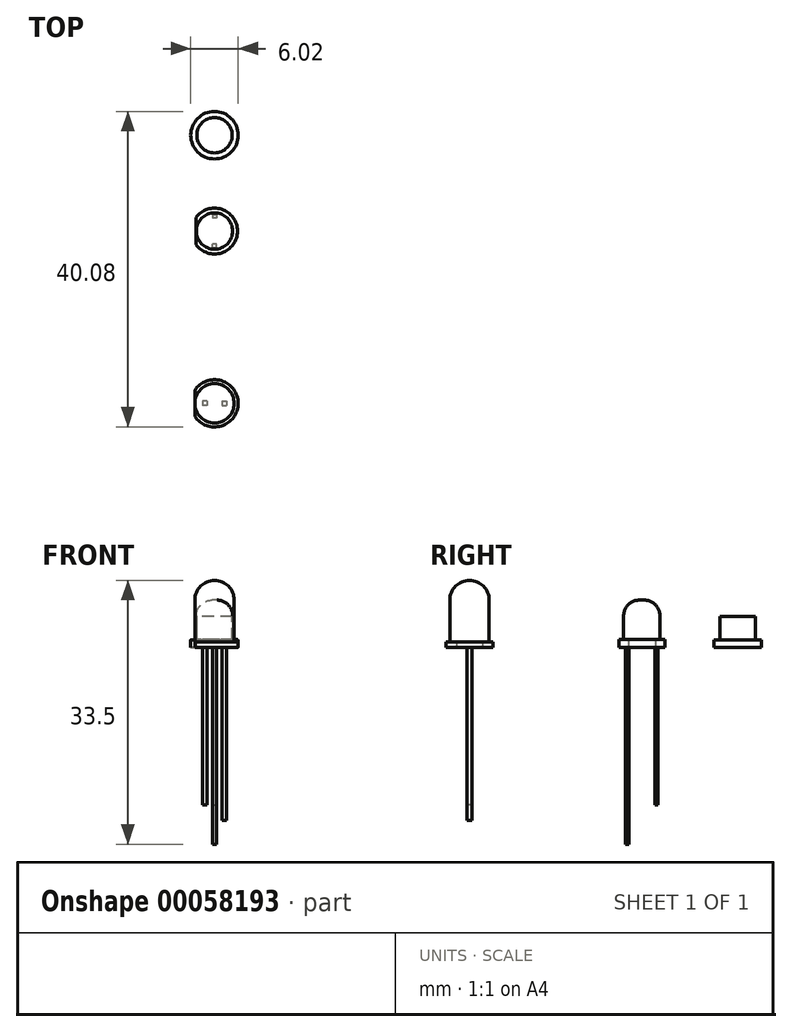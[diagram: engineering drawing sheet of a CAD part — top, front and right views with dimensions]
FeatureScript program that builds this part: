
annotation { "Feature Type Name" : "Feature", "Feature Type Description" : "" }
export const myFeature = defineFeature(function(context is Context, id is Id, definition is map)
    precondition{}
    {
        {
            var Q0;
            Q0=qCreatedBy(makeId("Top.planeOp"),FACE);
            var sketch = newSketch(context, id + "F0", { "sketchPlane" : qUnion([Q0])});
            skCircle(sketch, "E0", {"center": v(0, 0) * mm, "radius": 2.5 * mm});
            skSolve(sketch);
        }
        {
            var Q0;
            Q0=qSketchRegion(id+"F0",true);
            extrude(context, id + "F1", {"entities" : qUnion([Q0]), "depth" : 6 * mm});
        }
        {
            var Q0;
            Q0=makeQuery(id+"F1.opExtrude","CAP_FACE",FACE,{"disambiguationData":[OSD([sQuery(id+"F0.wireOp",EDGE,"E0")])],"isStart":false});
            var sketch = newSketch(context, id + "F2", { "sketchPlane" : qUnion([Q0])});
            skLineSegment(sketch, "E1", {"start": v(0, -2.5) * mm, "end": v(0, 2.5) * mm});
            skArc(sketch, "E2", {"start": v(0, 2.5) * mm, "mid": v(-2.5, 0) * mm, "end": v(0, -2.5) * mm});
            skSolve(sketch);
        }
        {
            var Q0;
            Q0=qSketchRegion(id+"F2",true);
            var Q1;
            Q1=sQuery(id+"F2.wireOp",EDGE,"E1");
            revolve(context, id + "F3", {"operationType" : NewBodyOperationType.ADD, "entities" : qUnion([Q0]), "axis" : qUnion([Q1]), "revolveType" : RevolveType.FULL});
        }
        {
            var Q0;
            Q0=makeQuery(id+"F1.opExtrude","CAP_FACE",FACE,{"disambiguationData":[OSD([sQuery(id+"F0.wireOp",EDGE,"E0")])],"isStart":true});
            var sketch = newSketch(context, id + "F4", { "sketchPlane" : qUnion([Q0])});
            skArc(sketch, "E3.0", {"start": v(-2.5, -1.66) * mm, "mid": v(3, 0) * mm, "end": v(-2.5, 1.66) * mm});
            skLineSegment(sketch, "E4", {"start": v(-2.5, -1.66) * mm, "end": v(-2.5, 1.66) * mm});
            skSolve(sketch);
        }
        {
            var Q0;
            Q0=qSketchRegion(id+"F4",true);
            extrude(context, id + "F5", {"entities" : qUnion([Q0]), "operationType" : NewBodyOperationType.ADD, "oppositeDirection" : true, "depth" : .7 * mm});
        }
        {
            var Q0;
            Q0=makeQuery(id+"F5.boolean.opBoolean","MERGE",FACE,{"derivedFrom":[makeQuery(id+"F1.opExtrude","CAP_FACE",FACE,{"disambiguationData":[OSD([sQuery(id+"F0.wireOp",EDGE,"E0")])],"isStart":true}),makeQuery(id+"F5.opExtrude","CAP_FACE",FACE,{"disambiguationData":[OSD([sQuery(id+"F4.wireOp",EDGE,"E3.0"),sQuery(id+"F4.wireOp",EDGE,"E4")])],"isStart":true})]});
            var sketch = newSketch(context, id + "F6", { "sketchPlane" : qUnion([Q0])});
            skLineSegment(sketch, "E5.rect.bottom", {"start": v(0.95, -0.3) * mm, "end": v(1.55, -0.3) * mm});
            skLineSegment(sketch, "E5.rect.top", {"start": v(0.95, 0.3) * mm, "end": v(1.55, 0.3) * mm});
            skLineSegment(sketch, "E5.rect.left", {"start": v(0.95, -0.3) * mm, "end": v(0.95, 0.3) * mm});
            skLineSegment(sketch, "E5.rect.right", {"start": v(1.55, -0.3) * mm, "end": v(1.55, 0.3) * mm});
            skPoint(sketch, "E5.rect.middle", {"position": v(1.25, 0) * mm});
            skLineSegment(sketch, "E6.rect.bottom", {"start": v(-0.95, -0.3) * mm, "end": v(-1.55, -0.3) * mm});
            skLineSegment(sketch, "E6.rect.top", {"start": v(-0.95, 0.3) * mm, "end": v(-1.55, 0.3) * mm});
            skLineSegment(sketch, "E6.rect.left", {"start": v(-0.95, -0.3) * mm, "end": v(-0.95, 0.3) * mm});
            skLineSegment(sketch, "E6.rect.right", {"start": v(-1.55, -0.3) * mm, "end": v(-1.55, 0.3) * mm});
            skPoint(sketch, "E6.rect.middle", {"position": v(-1.25, 0) * mm});
            skLineSegment(sketch, "E7", {"start": v(1.55, -0.3) * mm, "end": v(0.95, 0.3) * mm, "construction": true});
            skLineSegment(sketch, "E8", {"start": v(1.55, 0.3) * mm, "end": v(0.95, -0.3) * mm, "construction": true});
            skLineSegment(sketch, "E9", {"start": v(-0.95, -0.3) * mm, "end": v(-1.55, 0.3) * mm, "construction": true});
            skLineSegment(sketch, "E10", {"start": v(-0.95, 0.3) * mm, "end": v(-1.55, -0.3) * mm, "construction": true});
            skLineSegment(sketch, "E11", {"start": v(1.25, 0) * mm, "end": v(-1.25, 0) * mm, "construction": true});
            skSolve(sketch);
        }
        {
            var Q0;
            Q0=qSketchRegion(id+"F6",true);
            extrude(context, id + "F7", {"entities" : qUnion([Q0]), "operationType" : NewBodyOperationType.ADD, "depth" : 20 * mm});
        }
        {
            var Q0;
            Q0=makeQuery(id+"F7.opExtrude","CAP_FACE",FACE,{"disambiguationData":[OSD([sQuery(id+"F6.wireOp",EDGE,"E5.rect.bottom"),sQuery(id+"F6.wireOp",EDGE,"E5.rect.top"),sQuery(id+"F6.wireOp",EDGE,"E5.rect.left"),sQuery(id+"F6.wireOp",EDGE,"E5.rect.right")])],"isStart":false});
            extrude(context, id + "F8", {"entities" : qUnion([Q0]), "operationType" : NewBodyOperationType.ADD, "depth" : 2 * mm});
        }
        {
            var Q0;
            Q0=qCreatedBy(makeId("Top.planeOp"),FACE);
            var sketch = newSketch(context, id + "F9", { "sketchPlane" : qUnion([Q0])});
            skCircle(sketch, "E12", {"center": v(7.44, 15.47) * mm, "radius": 4.08 * mm});
            skSolve(sketch);
        }
        {
            var Q0;
            Q0=makeQuery(id+"F9.imprint","IMPRINT",FACE,{"disambiguationData":[TD([[makeQuery(id+"F9.imprint","IMPRINT",EDGE,{"derivedFrom":sQuery(id+"F9.wireOp",EDGE,"E12")}),1.0]])]});
            extrude(context, id + "F10", {"entities" : qUnion([Q0]), "depth" : 0.62 * mm});
        }
        {
            var Q0;
            Q0=makeQuery(id+"F10.opExtrude","SWEPT_BODY",BODY,{"disambiguationData":[OSD([sQuery(id+"F9.wireOp",EDGE,"E12")])]});
            deleteBodies(context, id + "F11", {"entities" : qUnion([Q0])});
        }
        {
            var Q0;
            Q0=qCreatedBy(makeId("Top.planeOp"),FACE);
            var sketch = newSketch(context, id + "F12", { "sketchPlane" : qUnion([Q0])});
            skCircle(sketch, "E13", {"center": v(0, 21.89) * mm, "radius": 2.91 * mm});
            skSolve(sketch);
        }
        {
            var Q0;
            Q0=qSketchRegion(id+"F12",true);
            extrude(context, id + "F13", {"entities" : qUnion([Q0]), "depth" : 1 * mm});
        }
        {
            var Q0;
            Q0=makeQuery(id+"F13.opExtrude","CAP_FACE",FACE,{"disambiguationData":[OSD([sQuery(id+"F12.wireOp",EDGE,"E13")])],"isStart":false});
            var sketch = newSketch(context, id + "F14", { "sketchPlane" : qUnion([Q0])});
            skCircle(sketch, "E14", {"center": v(0, 21.89) * mm, "radius": 2.3 * mm});
            skSolve(sketch);
        }
        {
            var Q0;
            Q0=qSketchRegion(id+"F14",true);
            extrude(context, id + "F15", {"entities" : qUnion([Q0]), "operationType" : NewBodyOperationType.ADD, "depth" : 5 * mm});
        }
        {
            var Q0;
            Q0=makeQuery(id+"F15.opExtrude","CAP_EDGE",EDGE,{"disambiguationData":[OSD([sQuery(id+"F14.wireOp",EDGE,"E14")])],"isStart":false});
            fillet(context, id + "F16", {"entities" : qUnion([Q0]), "radius" : 2 * mm, "tangentPropagation" : true, "allowEdgeOverflow" : false});
        }
        {
            var Q0;
            Q0=makeQuery(id+"F13.opExtrude","CAP_FACE",FACE,{"disambiguationData":[OSD([sQuery(id+"F12.wireOp",EDGE,"E13")])],"isStart":true});
            var sketch = newSketch(context, id + "F17", { "sketchPlane" : qUnion([Q0])});
            skLineSegment(sketch, "E15.rect.bottom", {"start": v(-0.26, -23.96) * mm, "end": v(0.26, -23.96) * mm});
            skLineSegment(sketch, "E15.rect.left", {"start": v(-0.26, -23.96) * mm, "end": v(-0.26, -23.54) * mm});
            skLineSegment(sketch, "E15.rect.right", {"start": v(0.26, -23.96) * mm, "end": v(0.26, -23.54) * mm});
            skPoint(sketch, "E15.rect.middle", {"position": v(0, -21.89) * mm});
            skLineSegment(sketch, "E16", {"start": v(0.26, -23.54) * mm, "end": v(-0.26, -23.54) * mm});
            skLineSegment(sketch, "E17", {"start": v(-1.36, -21.89) * mm, "end": v(2.2, -21.89) * mm, "construction": true});
            skPoint(sketch, "E15.rect.top.end.orphan", {"position": v(0.26, -19.81) * mm});
            skPoint(sketch, "E15.rect.top.start.orphan", {"position": v(-0.26, -19.81) * mm});
            skLineSegment(sketch, "E18.0.MirrorCS", {"start": v(-0.26, -19.81) * mm, "end": v(-0.26, -20.23) * mm});
            skLineSegment(sketch, "E18.1.MirrorCS", {"start": v(-0.26, -19.81) * mm, "end": v(0.26, -19.81) * mm});
            skLineSegment(sketch, "E18.2.MirrorCS", {"start": v(0.26, -19.81) * mm, "end": v(0.26, -20.23) * mm});
            skLineSegment(sketch, "E18.3.MirrorCS", {"start": v(0.26, -20.23) * mm, "end": v(-0.26, -20.23) * mm});
            skSolve(sketch);
        }
        {
            var Q0;
            Q0=makeQuery(id+"F17.imprint","IMPRINT",FACE,{"disambiguationData":[TD([[makeQuery(id+"F17.imprint","IMPRINT",EDGE,{"derivedFrom":sQuery(id+"F17.wireOp",EDGE,"E18.0.MirrorCS")}),1.0]])]});
            extrude(context, id + "F18", {"entities" : qUnion([Q0]), "operationType" : NewBodyOperationType.ADD, "depth" : 25 * mm});
        }
        {
            var Q0;
            Q0=makeQuery(id+"F17.imprint","IMPRINT",FACE,{"disambiguationData":[TD([[makeQuery(id+"F17.imprint","IMPRINT",EDGE,{"derivedFrom":sQuery(id+"F17.wireOp",EDGE,"E15.rect.bottom")}),-1.0]])]});
            var sketch = newSketch(context, id + "F19", { "sketchPlane" : qUnion([Q0])});
            skLineSegment(sketch, "E19.0", {"start": v(-0.26, -23.96) * mm, "end": v(-0.26, -23.54) * mm});
            skLineSegment(sketch, "E20.0", {"start": v(-0.26, -23.96) * mm, "end": v(0.26, -23.96) * mm});
            skLineSegment(sketch, "E20.1", {"start": v(0.26, -23.96) * mm, "end": v(0.26, -23.54) * mm});
            skLineSegment(sketch, "E20.2", {"start": v(0.26, -23.54) * mm, "end": v(-0.26, -23.54) * mm});
            skSolve(sketch);
        }
        {
            var Q0;
            Q0=qSketchRegion(id+"F19",true);
            extrude(context, id + "F20", {"entities" : qUnion([Q0]), "operationType" : NewBodyOperationType.ADD, "depth" : 20 * mm});
        }
        {
            var Q0;
            Q0=makeQuery(id+"F17.imprint","IMPRINT",FACE,{"disambiguationData":[TD([[makeQuery(id+"F17.imprint","IMPRINT",EDGE,{"derivedFrom":sQuery(id+"F17.wireOp",EDGE,"E15.rect.bottom")}),-1.0]])]});
            var sketch = newSketch(context, id + "F21", { "sketchPlane" : qUnion([Q0])});
            skArc(sketch, "E21.0", {"start": v(-2.35, -20.16) * mm, "mid": v(-2.91, -21.89) * mm, "end": v(-2.35, -23.6) * mm});
            skLineSegment(sketch, "E22", {"start": v(-2.35, -23.6) * mm, "end": v(-2.35, -20.16) * mm});
            skSolve(sketch);
        }
        {
            var Q0;
            Q0=qSketchRegion(id+"F21",true);
            extrude(context, id + "F22", {"entities" : qUnion([Q0]), "operationType" : NewBodyOperationType.REMOVE, "oppositeDirection" : true, "depth" : 25 * mm});
        }
        {
            var Q0;
            Q0=qCreatedBy(makeId("Right.planeOp"),FACE);
            var sketch = newSketch(context, id + "F23", { "sketchPlane" : qUnion([Q0])});
            skLineSegment(sketch, "E23", {"start": v(31.05, 0) * mm, "end": v(31.05, 0.96) * mm});
            skLineSegment(sketch, "E24", {"start": v(31.05, 0.96) * mm, "end": v(31.82, 0.96) * mm});
            skLineSegment(sketch, "E25", {"start": v(31.82, 0.96) * mm, "end": v(31.82, 3.91) * mm});
            skLineSegment(sketch, "E26", {"start": v(31.82, 3.91) * mm, "end": v(34.06, 3.91) * mm});
            skLineSegment(sketch, "E27", {"start": v(34.06, 3.91) * mm, "end": v(34.06, 0) * mm});
            skLineSegment(sketch, "E28", {"start": v(34.06, 0) * mm, "end": v(31.05, 0) * mm});
            skLineSegment(sketch, "E29", {"start": v(34.06, 3.91) * mm, "end": v(34.06, -6.33) * mm, "construction": true});
            skSolve(sketch);
        }
        {
            var Q0;
            Q0=makeQuery(id+"F23.imprint","IMPRINT",FACE,{"disambiguationData":[TD([[makeQuery(id+"F23.imprint","IMPRINT",EDGE,{"derivedFrom":sQuery(id+"F23.wireOp",EDGE,"E23")}),-1.0]])]});
            var Q1;
            Q1=sQuery(id+"F23.wireOp",EDGE,"E29");
            revolve(context, id + "F24", {"entities" : qUnion([Q0]), "axis" : qUnion([Q1]), "revolveType" : RevolveType.FULL});
        }
    });
